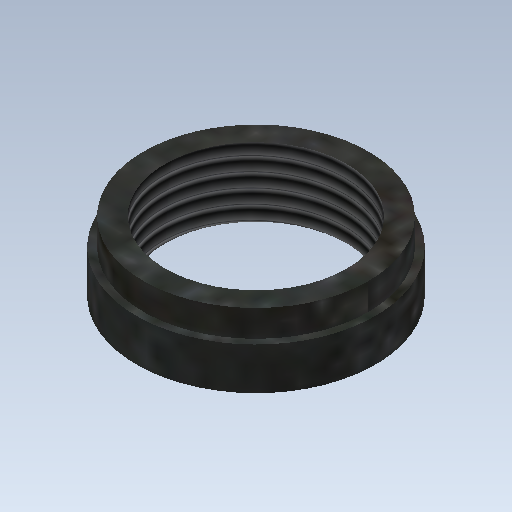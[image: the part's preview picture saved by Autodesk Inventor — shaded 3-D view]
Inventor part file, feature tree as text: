
AUTODESK INVENTOR PART (.ipt)
format: ipt  version: 2020 (Build 240168000, 168)  size: 172,032 bytes
history: native  units: mm
features: sketch x3, extrude x2, hole x1
ambient origin geometry x8: Origin, YZ Plane, XZ Plane, XY Plane, X Axis, Y Axis, Z Axis, Center Point
bodies: Solid1 (feature_tree)
feature tree (6):
  extrude  "Extrusion1"  Depth=3.0mm TaperAngle=0.0deg
  extrude  "Extrusion2"  Depth=1.9mm TaperAngle=0.0deg
  hole  "Hole1"  [1 undecoded]
  sketch  "Sketch1"  dims[d0=17.0mm d1=3.0mm d2=0.0mm]
  sketch  "Sketch2"  dims[d3=16.0mm d4=1.9mm d5=0.0mm]
  sketch  "Sketch3"  dims[d6=12.917mm d7=28.0mm d8=4.0mm d9=2.0mm d10=90.0deg d11=33.1mm d12=20.594885mm]
note: 1 required parameter value undecoded (feature->parameter linkage not recoverable at this tier; creation-order binding heuristic only, values carry confidence <= 0.55)
